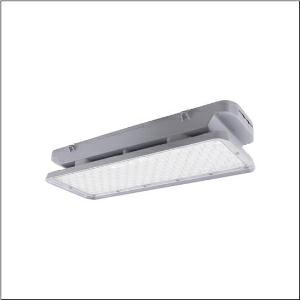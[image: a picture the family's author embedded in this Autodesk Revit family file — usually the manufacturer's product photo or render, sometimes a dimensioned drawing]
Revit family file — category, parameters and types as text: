
# Revit family: highbay_21-s_51hk41da4jca
name_source: partatom
category: Lighting Fixtures
units: mm (PartAtom-declared; Revit-internal decimal feet)

## family parameters
Cut with Voids When Loaded = No
Host = Face
Light Source = No
Part Type = Normal
Room Calculation Point = No
Round Connector Dimension = Use Diameter
Shared = No

## types (1)
- Highbay 21-S (1 x LED, 19100 lm, 107 W, 4000K)
    Apparent Load = 107 VA
    CIE Flux Codes = 87 97 99 100 100
    Color Rendering = 80
    Color Temperature = 4000K
    Default Elevation = 1800 mm
    Description = Highbay 21-S, LED high bay luminaire, primary light control with lens, of PC, primary optical cover: cover panel, light emission: direct distribution, primary light characteristic: symmetric, installation type: suspended mounting, surface-mounted, LED, rated luminous flux: 19.100lm, luminous efficacy: 159lm/W, light colour: 840, colour temperature: 4000K, control gear: ECG DALI, with terminal, 5-pole, max. 2.5mm², mains connection: 220..240V, AC, 50Hz, rated input power: 120W, housing, of diecast aluminium, coated, grey, length: 471mm, width: 172mm, height: 87mm, protection rating (complete): IP66, insulation class (complete): insulation class I (protective earthing), certification: CE, ENEC, UKCA, protection symbol: D, impact resistance: IK08, permissible operating ambient temperature: -30..+55°C, corresponds to IFS (International Featured Standards) requirements for safety and quality in the food industry, LABS conformity tested according to VDMA 24364:2018-05, packaging unit: 1 piece
    Height = 89 mm
    Lamp = 1 x LED
    Lamp Light Flux = 19100 lm
    Lamp Power = 107 W
    Lamp count = 1
    Length = 471 mm
    Luminous efficacy = 179 lm/W
    Manufacturer = Siteco
    ModVariant = No
    Model = 51HK41DA4JCA
    Mounting Place = Ceiling
    Mounting Type = Pendant
    Number of Poles = 1
    OnlyDefault = Yes
    Power Factor = 1
    Product Name = Highbay 21-S
    Product group = LED high bay luminaire
    ProductGroupID = 903
    Protection Class = Protection class I
    Protection Degree = IP 66
    RLX_Detail_Level = 1
    RLX_Emergency_Light_Flux = 0 lm
    RLX_Emergency_Type = 0
    RLX_Emergency_Type_DB = No
    RlxData = <blob elided: 21537 chars, md5=3862a56e>
    Socket = socket
    Standby Power = 0 W
    System Light Flux = 19100 lm
    System Power = 107 W
    Type Comments = Product without accessories
    Type Image = l_1276526.jpg
    URL = http://relux.com
    VarID = ---
    Voltage = 0 V
    Weight = 0.00 kg
    Width = 172 mm

## geometry (parser evidence)
native form markers: Blend x4, Sweep x10
no freeform markers — native parametric forms only
